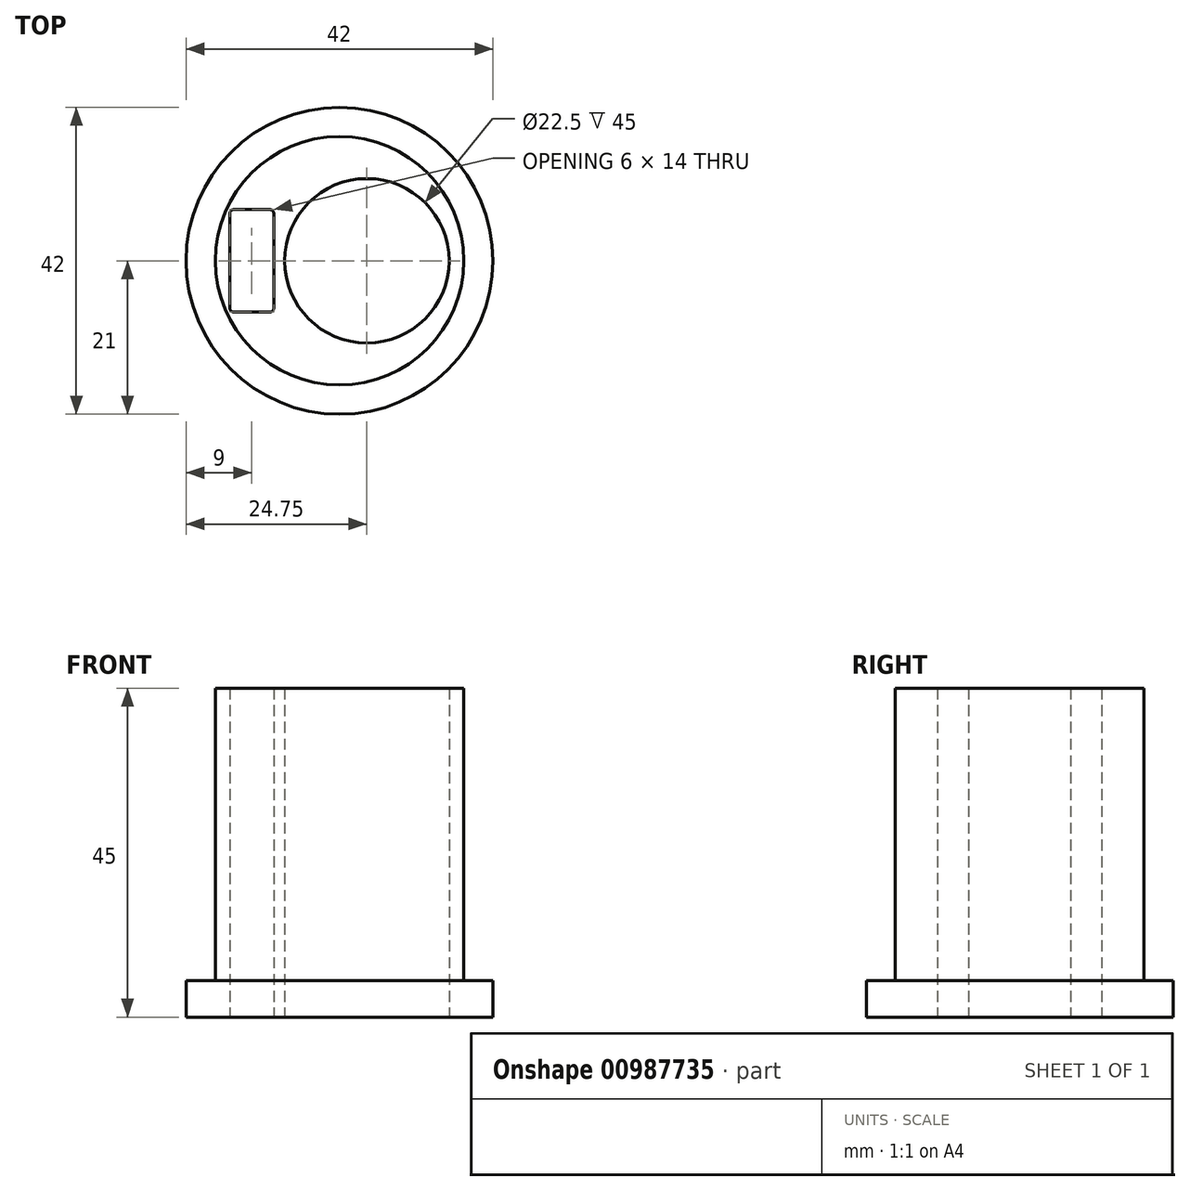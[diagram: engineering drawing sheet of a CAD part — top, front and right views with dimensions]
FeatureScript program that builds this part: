
annotation { "Feature Type Name" : "Feature", "Feature Type Description" : "" }
export const myFeature = defineFeature(function(context is Context, id is Id, definition is map)
    precondition{}
    {
        {
            var Q0;
            Q0=qCreatedBy(makeId("Top.planeOp"),FACE);
            var sketch = newSketch(context, id + "F0", { "sketchPlane" : qUnion([Q0])});
            skCircle(sketch, "E0", {"center": v(0, 0) * mm, "radius": 21 * mm});
            skCircle(sketch, "E1", {"center": v(0, 0) * mm, "radius": 17 * mm});
            skCircle(sketch, "E2", {"center": v(3.75, 0) * mm, "radius": 11.25 * mm});
            skLineSegment(sketch, "E3.bottom", {"start": v(-9.5, -7) * mm, "end": v(-14.5, -7) * mm});
            skLineSegment(sketch, "E3.top", {"start": v(-9.5, 7) * mm, "end": v(-14.5, 7) * mm});
            skLineSegment(sketch, "E3.left", {"start": v(-9, -6.5) * mm, "end": v(-9, 6.5) * mm});
            skLineSegment(sketch, "E3.right", {"start": v(-15, -6.5) * mm, "end": v(-15, 6.5) * mm});
            skPoint(sketch, "E3.middle", {"position": v(-12, 0) * mm});
            skPoint(sketch, "E4.visualSharp", {"position": v(-15, 7) * mm});
            skArc(sketch, "E4.filletArc", {"start": v(-14.5, 7) * mm, "mid": v(-14.85, 6.85) * mm, "end": v(-15, 6.5) * mm});
            skPoint(sketch, "E5.visualSharp", {"position": v(-9, 7) * mm});
            skArc(sketch, "E5.filletArc", {"start": v(-9, 6.5) * mm, "mid": v(-9.15, 6.85) * mm, "end": v(-9.5, 7) * mm});
            skPoint(sketch, "E6.visualSharp", {"position": v(-9, -7) * mm});
            skArc(sketch, "E6.filletArc", {"start": v(-9.5, -7) * mm, "mid": v(-9.15, -6.85) * mm, "end": v(-9, -6.5) * mm});
            skPoint(sketch, "E7.visualSharp", {"position": v(-15, -7) * mm});
            skArc(sketch, "E7.filletArc", {"start": v(-15, -6.5) * mm, "mid": v(-14.85, -6.85) * mm, "end": v(-14.5, -7) * mm});
            skSolve(sketch);
        }
        {
            var Q0;
            Q0=makeQuery(id+"F0.imprint","IMPRINT",FACE,{"disambiguationData":[TD([[makeQuery(id+"F0.imprint","IMPRINT",EDGE,{"derivedFrom":sQuery(id+"F0.wireOp",EDGE,"E1")}),1.0]])]});
            extrude(context, id + "F1", {"entities" : qUnion([Q0]), "depth" : 45 * mm, "offsetDistance" : 25 * mm});
        }
        {
            var Q0;
            Q0=makeQuery(id+"F0.imprint","IMPRINT",FACE,{"disambiguationData":[TD([[makeQuery(id+"F0.imprint","IMPRINT",EDGE,{"derivedFrom":sQuery(id+"F0.wireOp",EDGE,"E0")}),1.0]])]});
            extrude(context, id + "F2", {"entities" : qUnion([Q0]), "operationType" : NewBodyOperationType.ADD, "depth" : 5 * mm, "offsetDistance" : 25 * mm});
        }
    });
